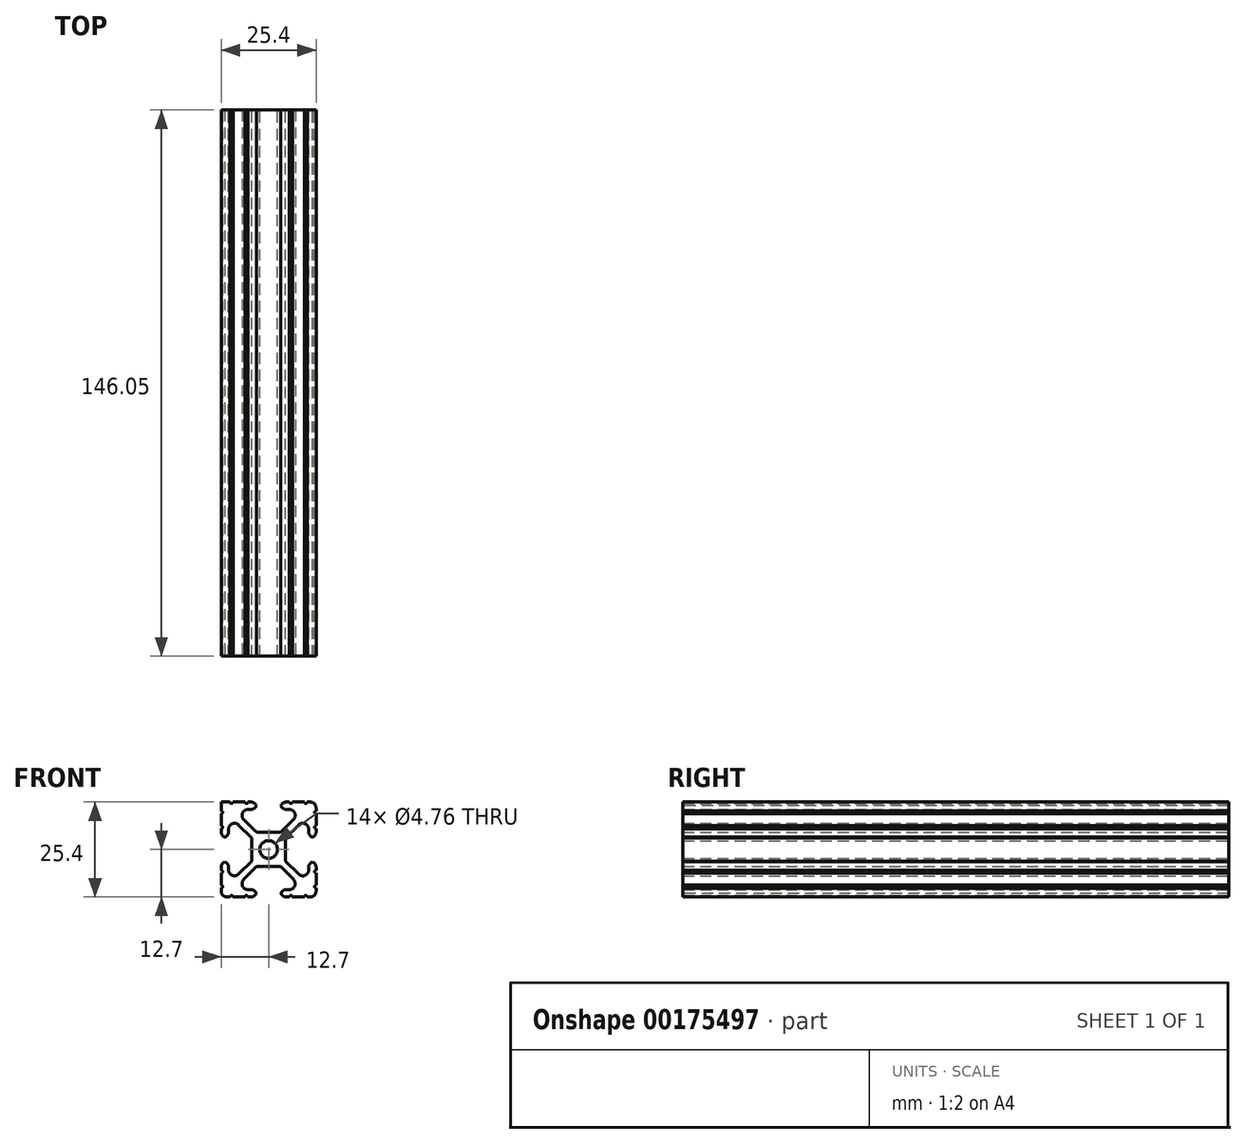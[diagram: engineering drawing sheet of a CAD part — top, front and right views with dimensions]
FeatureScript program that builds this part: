
annotation { "Feature Type Name" : "Feature", "Feature Type Description" : "" }
export const myFeature = defineFeature(function(context is Context, id is Id, definition is map)
    precondition{}
    {
        {
            var Q0;
            Q0=qCreatedBy(makeId("Front.planeOp"),FACE);
            var sketch = newSketch(context, id + "F0", { "sketchPlane" : qUnion([Q0])});
            skCircle(sketch, "E0", {"center": v(0, 0) * mm, "radius": 2.38 * mm});
            skLineSegment(sketch, "E1.bottom", {"start": v(-12.7, 12.7) * mm, "end": v(12.7, 12.7) * mm});
            skLineSegment(sketch, "E1.top", {"start": v(-12.7, -12.7) * mm, "end": v(12.7, -12.7) * mm});
            skLineSegment(sketch, "E1.left", {"start": v(-12.7, 12.7) * mm, "end": v(-12.7, -12.7) * mm});
            skLineSegment(sketch, "E1.right", {"start": v(12.7, 12.7) * mm, "end": v(12.7, -12.7) * mm});
            skPoint(sketch, "E2", {"position": v(0, 12.7) * mm});
            skLineSegment(sketch, "E3", {"start": v(0, 12.7) * mm, "end": v(-3.18, 12.7) * mm});
            skLineSegment(sketch, "E4", {"start": v(0, 12.7) * mm, "end": v(3.17, 12.7) * mm});
            skLineSegment(sketch, "E5", {"start": v(-3.18, 12.7) * mm, "end": v(-3.18, 10.72) * mm});
            skPoint(sketch, "E6", {"position": v(-12.7, 0) * mm});
            skLineSegment(sketch, "E7", {"start": v(-12.7, 0) * mm, "end": v(-12.7, 3.18) * mm});
            skLineSegment(sketch, "E8.MirrorCS", {"start": v(-12.7, 0) * mm, "end": v(-12.7, -3.18) * mm});
            skLineSegment(sketch, "E9", {"start": v(-12.7, 3.18) * mm, "end": v(-10.72, 3.18) * mm});
            skLineSegment(sketch, "E10.MirrorCS", {"start": v(-12.7, -3.18) * mm, "end": v(-10.72, -3.18) * mm});
            skLineSegment(sketch, "E11.MirrorCS", {"start": v(3.18, 12.7) * mm, "end": v(3.18, 10.72) * mm});
            skLineSegment(sketch, "E12.bottom", {"start": v(-12.7, 12.7) * mm, "end": v(-7.14, 12.7) * mm});
            skLineSegment(sketch, "E13", {"start": v(-3.18, 10.72) * mm, "end": v(-7.14, 10.72) * mm});
            skLineSegment(sketch, "E14", {"start": v(-10.72, 3.18) * mm, "end": v(-10.72, 7.14) * mm});
            skLineSegment(sketch, "E15", {"start": v(-12.7, 11.22) * mm, "end": v(-11.37, 12.7) * mm});
            skPoint(sketch, "E16", {"position": v(-1.52, -1.52) * mm});
            skPoint(sketch, "E17", {"position": v(-2.92, -2.92) * mm});
            skLineSegment(sketch, "E18", {"start": v(0, 0) * mm, "end": v(0.7, 0.7) * mm});
            skLineSegment(sketch, "E19", {"start": v(0, 0) * mm, "end": v(-0.7, -0.7) * mm});
            skLineSegment(sketch, "E20", {"start": v(-0.7, -0.7) * mm, "end": v(-12.7, 11.22) * mm});
            skLineSegment(sketch, "E21", {"start": v(-11.37, 12.7) * mm, "end": v(0.7, 0.7) * mm});
            skLineSegment(sketch, "E22.MirrorCS", {"start": v(3.18, 10.72) * mm, "end": v(7.14, 10.72) * mm});
            skLineSegment(sketch, "E23.MirrorCS", {"start": v(10.72, 3.18) * mm, "end": v(10.72, 7.14) * mm});
            skLineSegment(sketch, "E24.MirrorCS", {"start": v(12.7, 3.18) * mm, "end": v(10.72, 3.18) * mm});
            skLineSegment(sketch, "E25.MirrorCS", {"start": v(0.7, -0.7) * mm, "end": v(12.7, 11.22) * mm});
            skLineSegment(sketch, "E26.MirrorCS", {"start": v(11.37, 12.7) * mm, "end": v(-0.7, 0.7) * mm});
            skLineSegment(sketch, "E27.MirrorCS", {"start": v(3.18, -10.72) * mm, "end": v(7.14, -10.72) * mm});
            skLineSegment(sketch, "E28.MirrorCS", {"start": v(3.18, -12.7) * mm, "end": v(3.18, -10.72) * mm});
            skLineSegment(sketch, "E29.MirrorCS", {"start": v(11.37, -12.7) * mm, "end": v(-0.7, -0.7) * mm});
            skLineSegment(sketch, "E30.MirrorCS", {"start": v(0.7, 0.7) * mm, "end": v(12.7, -11.22) * mm});
            skLineSegment(sketch, "E31.MirrorCS", {"start": v(10.72, -3.18) * mm, "end": v(10.72, -7.14) * mm});
            skLineSegment(sketch, "E32.MirrorCS", {"start": v(12.7, -3.18) * mm, "end": v(10.72, -3.18) * mm});
            skLineSegment(sketch, "E33.MirrorCS", {"start": v(-3.18, -12.7) * mm, "end": v(-3.18, -10.72) * mm});
            skLineSegment(sketch, "E34.MirrorCS", {"start": v(-3.18, -10.72) * mm, "end": v(-7.14, -10.72) * mm});
            skLineSegment(sketch, "E35.MirrorCS", {"start": v(-11.37, -12.7) * mm, "end": v(0.7, -0.7) * mm});
            skLineSegment(sketch, "E36.MirrorCS", {"start": v(-0.7, 0.7) * mm, "end": v(-12.7, -11.22) * mm});
            skLineSegment(sketch, "E37.MirrorCS", {"start": v(-10.72, -3.18) * mm, "end": v(-10.72, -7.14) * mm});
            skLineSegment(sketch, "E38.bottom", {"start": v(-4.56, 4.56) * mm, "end": v(4.56, 4.56) * mm});
            skLineSegment(sketch, "E38.top", {"start": v(-4.56, -4.56) * mm, "end": v(4.56, -4.56) * mm});
            skLineSegment(sketch, "E38.left", {"start": v(-4.56, 4.56) * mm, "end": v(-4.56, -4.56) * mm});
            skLineSegment(sketch, "E38.right", {"start": v(4.56, 4.56) * mm, "end": v(4.56, -4.56) * mm});
            skPoint(sketch, "E39", {"position": v(10.32, 12.7) * mm});
            skPoint(sketch, "E40", {"position": v(9.53, 12.7) * mm});
            skArc(sketch, "E41", {"start": v(9.53, 12.7) * mm, "mid": v(9.92, 12.3) * mm, "end": v(10.32, 12.7) * mm});
            skPoint(sketch, "E42", {"position": v(6.35, 12.7) * mm});
            skPoint(sketch, "E43", {"position": v(5.56, 12.7) * mm});
            skArc(sketch, "E44", {"start": v(5.56, 12.7) * mm, "mid": v(5.95, 12.3) * mm, "end": v(6.35, 12.7) * mm});
            skArc(sketch, "E45.MirrorCS", {"start": v(9.53, -12.7) * mm, "mid": v(9.92, -12.3) * mm, "end": v(10.32, -12.7) * mm});
            skArc(sketch, "E46.MirrorCS", {"start": v(5.56, -12.7) * mm, "mid": v(5.95, -12.3) * mm, "end": v(6.35, -12.7) * mm});
            skArc(sketch, "E47.MirrorCS", {"start": v(-5.56, -12.7) * mm, "mid": v(-5.95, -12.3) * mm, "end": v(-6.35, -12.7) * mm});
            skArc(sketch, "E48.MirrorCS", {"start": v(-9.53, -12.7) * mm, "mid": v(-9.92, -12.3) * mm, "end": v(-10.32, -12.7) * mm});
            skArc(sketch, "E49.MirrorCS", {"start": v(-5.56, 12.7) * mm, "mid": v(-5.95, 12.3) * mm, "end": v(-6.35, 12.7) * mm});
            skArc(sketch, "E50.MirrorCS", {"start": v(-9.53, 12.7) * mm, "mid": v(-9.92, 12.3) * mm, "end": v(-10.32, 12.7) * mm});
            skPoint(sketch, "E51", {"position": v(12.7, 10.32) * mm});
            skPoint(sketch, "E52", {"position": v(12.7, 9.53) * mm});
            skPoint(sketch, "E53", {"position": v(12.7, 6.35) * mm});
            skPoint(sketch, "E54", {"position": v(12.7, 5.56) * mm});
            skArc(sketch, "E55", {"start": v(12.7, 10.32) * mm, "mid": v(12.3, 9.92) * mm, "end": v(12.7, 9.53) * mm});
            skArc(sketch, "E56", {"start": v(12.7, 6.35) * mm, "mid": v(12.3, 5.95) * mm, "end": v(12.7, 5.56) * mm});
            skArc(sketch, "E57.MirrorCS", {"start": v(-12.7, 10.32) * mm, "mid": v(-12.3, 9.92) * mm, "end": v(-12.7, 9.53) * mm});
            skArc(sketch, "E58.MirrorCS", {"start": v(-12.7, 6.35) * mm, "mid": v(-12.3, 5.95) * mm, "end": v(-12.7, 5.56) * mm});
            skArc(sketch, "E59.MirrorCS", {"start": v(-12.7, -6.35) * mm, "mid": v(-12.3, -5.95) * mm, "end": v(-12.7, -5.56) * mm});
            skArc(sketch, "E60.MirrorCS", {"start": v(-12.7, -10.32) * mm, "mid": v(-12.3, -9.92) * mm, "end": v(-12.7, -9.53) * mm});
            skArc(sketch, "E61.MirrorCS", {"start": v(12.7, -6.35) * mm, "mid": v(12.3, -5.95) * mm, "end": v(12.7, -5.56) * mm});
            skArc(sketch, "E62.MirrorCS", {"start": v(12.7, -10.32) * mm, "mid": v(12.3, -9.92) * mm, "end": v(12.7, -9.53) * mm});
            skLineSegment(sketch, "E63", {"start": v(-10.72, 7.14) * mm, "end": v(-10.72, 9.25) * mm});
            skLineSegment(sketch, "E64", {"start": v(-7.14, 10.72) * mm, "end": v(-9.38, 10.72) * mm});
            skLineSegment(sketch, "E65", {"start": v(7.14, 10.72) * mm, "end": v(9.38, 10.72) * mm});
            skLineSegment(sketch, "E66", {"start": v(10.72, 7.14) * mm, "end": v(10.72, 9.25) * mm});
            skLineSegment(sketch, "E67", {"start": v(7.14, -10.72) * mm, "end": v(9.38, -10.72) * mm});
            skLineSegment(sketch, "E68", {"start": v(10.72, -7.14) * mm, "end": v(10.72, -9.25) * mm});
            skLineSegment(sketch, "E69", {"start": v(-10.72, -7.14) * mm, "end": v(-10.72, -9.25) * mm});
            skLineSegment(sketch, "E70", {"start": v(-7.14, -10.72) * mm, "end": v(-9.38, -10.72) * mm});
            skSolve(sketch);
        }
        {
            var Q0;
            {var subQ0=sQuery(id+"F0.wireOp",EDGE,"E26.MirrorCS");var subQ1=sQuery(id+"F0.wireOp",EDGE,"E0");var subQ2=makeQuery(id+"F0.imprint","INTERSECT",VERTEX,{"derivedFrom":[subQ1,subQ0]});Q0=makeQuery(id+"F0.imprint","IMPRINT",FACE,{"disambiguationData":[TD([[makeQuery(id+"F0.imprint","IMPRINT",EDGE,{"disambiguationData":[TD([[subQ2,-1.0]])],"derivedFrom":subQ1}),-1.0]])]});}
            var Q1;
            {var subQ3=sQuery(id+"F0.wireOp",EDGE,"E21");var subQ5=sQuery(id+"F0.wireOp",EDGE,"E0");var subQ6=makeQuery(id+"F0.imprint","INTERSECT",VERTEX,{"derivedFrom":[subQ5,subQ3]});Q1=makeQuery(id+"F0.imprint","IMPRINT",FACE,{"disambiguationData":[TD([[makeQuery(id+"F0.imprint","IMPRINT",EDGE,{"disambiguationData":[TD([[subQ6,-1.0]])],"derivedFrom":subQ5}),-1.0]])]});}
            var Q2;
            {var subQ0=sQuery(id+"F0.wireOp",EDGE,"E20");var subQ1=sQuery(id+"F0.wireOp",EDGE,"E0");var subQ2=makeQuery(id+"F0.imprint","INTERSECT",VERTEX,{"derivedFrom":[subQ1,subQ0]});Q2=makeQuery(id+"F0.imprint","IMPRINT",FACE,{"disambiguationData":[TD([[makeQuery(id+"F0.imprint","IMPRINT",EDGE,{"disambiguationData":[TD([[subQ2,-1.0]])],"derivedFrom":subQ1}),-1.0]])]});}
            var Q3;
            {var subQ5=sQuery(id+"F0.wireOp",EDGE,"E0");var subQ7=sQuery(id+"F0.wireOp",EDGE,"E36.MirrorCS");var subQ8=makeQuery(id+"F0.imprint","INTERSECT",VERTEX,{"derivedFrom":[subQ5,subQ7]});Q3=makeQuery(id+"F0.imprint","IMPRINT",FACE,{"disambiguationData":[TD([[makeQuery(id+"F0.imprint","IMPRINT",EDGE,{"disambiguationData":[TD([[subQ8,-1.0]])],"derivedFrom":subQ5}),-1.0]])]});}
            var Q4;
            {var subQ0=sQuery(id+"F0.wireOp",EDGE,"E35.MirrorCS");var subQ1=sQuery(id+"F0.wireOp",EDGE,"E0");var subQ2=makeQuery(id+"F0.imprint","INTERSECT",VERTEX,{"derivedFrom":[subQ1,subQ0]});Q4=makeQuery(id+"F0.imprint","IMPRINT",FACE,{"disambiguationData":[TD([[makeQuery(id+"F0.imprint","IMPRINT",EDGE,{"disambiguationData":[TD([[subQ2,-1.0]])],"derivedFrom":subQ1}),-1.0]])]});}
            var Q5;
            {var subQ3=sQuery(id+"F0.wireOp",EDGE,"E29.MirrorCS");var subQ6=sQuery(id+"F0.wireOp",EDGE,"E0");var subQ9=makeQuery(id+"F0.imprint","INTERSECT",VERTEX,{"derivedFrom":[subQ6,subQ3]});Q5=makeQuery(id+"F0.imprint","IMPRINT",FACE,{"disambiguationData":[TD([[makeQuery(id+"F0.imprint","IMPRINT",EDGE,{"disambiguationData":[TD([[subQ9,-1.0]])],"derivedFrom":subQ6}),-1.0]])]});}
            var Q6;
            {var subQ0=sQuery(id+"F0.wireOp",EDGE,"E25.MirrorCS");var subQ1=sQuery(id+"F0.wireOp",EDGE,"E0");var subQ2=makeQuery(id+"F0.imprint","INTERSECT",VERTEX,{"derivedFrom":[subQ1,subQ0]});Q6=makeQuery(id+"F0.imprint","IMPRINT",FACE,{"disambiguationData":[TD([[makeQuery(id+"F0.imprint","IMPRINT",EDGE,{"disambiguationData":[TD([[subQ2,1.0]])],"derivedFrom":subQ1}),-1.0]])]});}
            var Q7;
            {var subQ3=sQuery(id+"F0.wireOp",EDGE,"E26.MirrorCS");var subQ7=sQuery(id+"F0.wireOp",EDGE,"E0");var subQ8=makeQuery(id+"F0.imprint","INTERSECT",VERTEX,{"derivedFrom":[subQ7,subQ3]});Q7=makeQuery(id+"F0.imprint","IMPRINT",FACE,{"disambiguationData":[TD([[makeQuery(id+"F0.imprint","IMPRINT",EDGE,{"disambiguationData":[TD([[subQ8,1.0]])],"derivedFrom":subQ7}),-1.0]])]});}
            var Q8;
            {var subQ1=sQuery(id+"F0.wireOp",EDGE,"E1.right");var subQ6=sQuery(id+"F0.wireOp",EDGE,"E1.bottom");var subQ7=makeQuery(id+"F0.imprint","INTERSECT",VERTEX,{"derivedFrom":[subQ6,subQ1]});Q8=makeQuery(id+"F0.imprint","IMPRINT",FACE,{"disambiguationData":[TD([[makeQuery(id+"F0.imprint","IMPRINT",EDGE,{"disambiguationData":[TD([[subQ7,1.0]])],"derivedFrom":subQ6}),-1.0]])]});}
            var Q9;
            Q9=makeQuery(id+"F0.imprint","IMPRINT",FACE,{"disambiguationData":[TD([[makeQuery(id+"F0.imprint","IMPRINT",EDGE,{"derivedFrom":sQuery(id+"F0.wireOp",EDGE,"E23.MirrorCS")}),-1.0]])]});
            var Q10;
            {var subQ0=sQuery(id+"F0.wireOp",EDGE,"E11.MirrorCS");Q10=makeQuery(id+"F0.imprint","IMPRINT",FACE,{"disambiguationData":[TD([[makeQuery(id+"F0.imprint","IMPRINT",EDGE,{"derivedFrom":subQ0}),1.0]])]});}
            var Q11;
            {var subQ4=sQuery(id+"F0.wireOp",EDGE,"E5");Q11=makeQuery(id+"F0.imprint","IMPRINT",FACE,{"disambiguationData":[TD([[makeQuery(id+"F0.imprint","IMPRINT",EDGE,{"derivedFrom":subQ4}),-1.0]])]});}
            var Q12;
            {var subQ1=sQuery(id+"F0.wireOp",EDGE,"E15");Q12=makeQuery(id+"F0.imprint","IMPRINT",FACE,{"disambiguationData":[TD([[makeQuery(id+"F0.imprint","IMPRINT",EDGE,{"derivedFrom":subQ1}),-1.0]])]});}
            var Q13;
            {var subQ3=sQuery(id+"F0.wireOp",EDGE,"E15");Q13=makeQuery(id+"F0.imprint","IMPRINT",FACE,{"disambiguationData":[TD([[makeQuery(id+"F0.imprint","IMPRINT",EDGE,{"derivedFrom":subQ3}),1.0]])]});}
            var Q14;
            {var subQ0=sQuery(id+"F0.wireOp",EDGE,"E9");Q14=makeQuery(id+"F0.imprint","IMPRINT",FACE,{"disambiguationData":[TD([[makeQuery(id+"F0.imprint","IMPRINT",EDGE,{"derivedFrom":subQ0}),1.0]])]});}
            var Q15;
            {var subQ0=sQuery(id+"F0.wireOp",EDGE,"E10.MirrorCS");Q15=makeQuery(id+"F0.imprint","IMPRINT",FACE,{"disambiguationData":[TD([[makeQuery(id+"F0.imprint","IMPRINT",EDGE,{"derivedFrom":subQ0}),-1.0]])]});}
            var Q16;
            {var subQ0=sQuery(id+"F0.wireOp",EDGE,"E10.MirrorCS");Q16=makeQuery(id+"F0.imprint","IMPRINT",FACE,{"disambiguationData":[TD([[makeQuery(id+"F0.imprint","IMPRINT",EDGE,{"derivedFrom":subQ0}),-1.0]])]});}
            var Q17;
            {var subQ4=sQuery(id+"F0.wireOp",EDGE,"E1.top");var subQ6=sQuery(id+"F0.wireOp",EDGE,"E1.left");var subQ7=makeQuery(id+"F0.imprint","INTERSECT",VERTEX,{"derivedFrom":[subQ4,subQ6]});Q17=makeQuery(id+"F0.imprint","IMPRINT",FACE,{"disambiguationData":[TD([[makeQuery(id+"F0.imprint","IMPRINT",EDGE,{"disambiguationData":[TD([[subQ7,-1.0]])],"derivedFrom":subQ4}),1.0]])]});}
            var Q18;
            {var subQ0=sQuery(id+"F0.wireOp",EDGE,"E33.MirrorCS");Q18=makeQuery(id+"F0.imprint","IMPRINT",FACE,{"disambiguationData":[TD([[makeQuery(id+"F0.imprint","IMPRINT",EDGE,{"derivedFrom":subQ0}),1.0]])]});}
            var Q19;
            Q19=makeQuery(id+"F0.imprint","IMPRINT",FACE,{"disambiguationData":[TD([[makeQuery(id+"F0.imprint","IMPRINT",EDGE,{"derivedFrom":sQuery(id+"F0.wireOp",EDGE,"E27.MirrorCS")}),-1.0]])]});
            var Q20;
            {var subQ1=sQuery(id+"F0.wireOp",EDGE,"E1.top");var subQ6=sQuery(id+"F0.wireOp",EDGE,"E1.right");var subQ7=makeQuery(id+"F0.imprint","INTERSECT",VERTEX,{"derivedFrom":[subQ1,subQ6]});Q20=makeQuery(id+"F0.imprint","IMPRINT",FACE,{"disambiguationData":[TD([[makeQuery(id+"F0.imprint","IMPRINT",EDGE,{"disambiguationData":[TD([[subQ7,1.0]])],"derivedFrom":subQ1}),1.0]])]});}
            var Q21;
            Q21=makeQuery(id+"F0.imprint","IMPRINT",FACE,{"disambiguationData":[TD([[makeQuery(id+"F0.imprint","IMPRINT",EDGE,{"derivedFrom":sQuery(id+"F0.wireOp",EDGE,"E31.MirrorCS")}),1.0]])]});
            var Q22;
            Q22=makeQuery(id+"F0.imprint","IMPRINT",FACE,{"disambiguationData":[TD([[makeQuery(id+"F0.imprint","IMPRINT",EDGE,{"derivedFrom":sQuery(id+"F0.wireOp",EDGE,"E31.MirrorCS")}),1.0]])]});
            extrude(context, id + "F1", {"entities" : qUnion([Q0, Q1, Q2, Q3, Q4, Q5, Q6, Q7, Q8, Q9, Q10, Q11, Q12, Q13, Q14, Q15, Q16, Q17, Q18, Q19, Q20, Q21, Q22]), "depth" : 146.05 * mm});
        }
        {
            var Q0;
            Q0=makeQuery(id+"F1.opExtrude","SWEPT_EDGE",EDGE,{"disambiguationData":[OSD([sQuery(id+"F0.wireOp",EDGE,"E12.bottom"),sQuery(id+"F0.wireOp",EDGE,"E12.left")])]});
            var Q1;
            Q1=makeQuery(id+"F1.opExtrude","SWEPT_EDGE",EDGE,{"disambiguationData":[OSD([sQuery(id+"F0.wireOp",EDGE,"E1.top"),sQuery(id+"F0.wireOp",EDGE,"E1.left")])]});
            var Q2;
            Q2=makeQuery(id+"F1.opExtrude","SWEPT_EDGE",EDGE,{"disambiguationData":[OSD([sQuery(id+"F0.wireOp",EDGE,"E1.top"),sQuery(id+"F0.wireOp",EDGE,"E1.right")])]});
            var Q3;
            Q3=makeQuery(id+"F1.opExtrude","SWEPT_EDGE",EDGE,{"disambiguationData":[OSD([sQuery(id+"F0.wireOp",EDGE,"E1.bottom"),sQuery(id+"F0.wireOp",EDGE,"E1.right")])]});
            var Q4;
            Q4=makeQuery(id+"F1.opExtrude","SWEPT_EDGE",EDGE,{"disambiguationData":[OSD([sQuery(id+"F0.wireOp",EDGE,"E1.left"),sQuery(id+"F0.wireOp",EDGE,"E7"),sQuery(id+"F0.wireOp",EDGE,"E9")])]});
            var Q5;
            Q5=makeQuery(id+"F1.opExtrude","SWEPT_EDGE",EDGE,{"disambiguationData":[OSD([sQuery(id+"F0.wireOp",EDGE,"E1.left"),sQuery(id+"F0.wireOp",EDGE,"E8.MirrorCS"),sQuery(id+"F0.wireOp",EDGE,"E10.MirrorCS")])]});
            var Q6;
            Q6=makeQuery(id+"F1.opExtrude","SWEPT_EDGE",EDGE,{"disambiguationData":[OSD([sQuery(id+"F0.wireOp",EDGE,"E9"),sQuery(id+"F0.wireOp",EDGE,"E14")])]});
            var Q7;
            Q7=makeQuery(id+"F1.opExtrude","SWEPT_EDGE",EDGE,{"disambiguationData":[OSD([sQuery(id+"F0.wireOp",EDGE,"E10.MirrorCS"),sQuery(id+"F0.wireOp",EDGE,"E37.MirrorCS")])]});
            var Q8;
            Q8=makeQuery(id+"F1.opExtrude","SWEPT_EDGE",EDGE,{"disambiguationData":[OSD([sQuery(id+"F0.wireOp",EDGE,"E33.MirrorCS"),sQuery(id+"F0.wireOp",EDGE,"E34.MirrorCS")])]});
            var Q9;
            Q9=makeQuery(id+"F1.opExtrude","SWEPT_EDGE",EDGE,{"disambiguationData":[OSD([sQuery(id+"F0.wireOp",EDGE,"E1.top"),sQuery(id+"F0.wireOp",EDGE,"E33.MirrorCS")])]});
            var Q10;
            Q10=makeQuery(id+"F1.opExtrude","SWEPT_EDGE",EDGE,{"disambiguationData":[OSD([sQuery(id+"F0.wireOp",EDGE,"E1.top"),sQuery(id+"F0.wireOp",EDGE,"E28.MirrorCS")])]});
            var Q11;
            Q11=makeQuery(id+"F1.opExtrude","SWEPT_EDGE",EDGE,{"disambiguationData":[OSD([sQuery(id+"F0.wireOp",EDGE,"E27.MirrorCS"),sQuery(id+"F0.wireOp",EDGE,"E28.MirrorCS")])]});
            var Q12;
            Q12=makeQuery(id+"F1.opExtrude","SWEPT_EDGE",EDGE,{"disambiguationData":[OSD([sQuery(id+"F0.wireOp",EDGE,"E1.right"),sQuery(id+"F0.wireOp",EDGE,"E32.MirrorCS")])]});
            var Q13;
            Q13=makeQuery(id+"F1.opExtrude","SWEPT_EDGE",EDGE,{"disambiguationData":[OSD([sQuery(id+"F0.wireOp",EDGE,"E1.right"),sQuery(id+"F0.wireOp",EDGE,"E24.MirrorCS")])]});
            var Q14;
            Q14=makeQuery(id+"F1.opExtrude","SWEPT_EDGE",EDGE,{"disambiguationData":[OSD([sQuery(id+"F0.wireOp",EDGE,"E31.MirrorCS"),sQuery(id+"F0.wireOp",EDGE,"E32.MirrorCS")])]});
            var Q15;
            Q15=makeQuery(id+"F1.opExtrude","SWEPT_EDGE",EDGE,{"disambiguationData":[OSD([sQuery(id+"F0.wireOp",EDGE,"E23.MirrorCS"),sQuery(id+"F0.wireOp",EDGE,"E24.MirrorCS")])]});
            var Q16;
            Q16=makeQuery(id+"F1.opExtrude","SWEPT_EDGE",EDGE,{"disambiguationData":[OSD([sQuery(id+"F0.wireOp",EDGE,"E5"),sQuery(id+"F0.wireOp",EDGE,"E13")])]});
            var Q17;
            Q17=makeQuery(id+"F1.opExtrude","SWEPT_EDGE",EDGE,{"disambiguationData":[OSD([sQuery(id+"F0.wireOp",EDGE,"E1.bottom"),sQuery(id+"F0.wireOp",EDGE,"E3"),sQuery(id+"F0.wireOp",EDGE,"E5")])]});
            var Q18;
            Q18=makeQuery(id+"F1.opExtrude","SWEPT_EDGE",EDGE,{"disambiguationData":[OSD([sQuery(id+"F0.wireOp",EDGE,"E1.bottom"),sQuery(id+"F0.wireOp",EDGE,"E4"),sQuery(id+"F0.wireOp",EDGE,"E11.MirrorCS")])]});
            var Q19;
            Q19=makeQuery(id+"F1.opExtrude","SWEPT_EDGE",EDGE,{"disambiguationData":[OSD([sQuery(id+"F0.wireOp",EDGE,"E11.MirrorCS"),sQuery(id+"F0.wireOp",EDGE,"E22.MirrorCS")])]});
            var Q20;
            Q20=makeQuery(id+"F1.opExtrude","SWEPT_EDGE",EDGE,{"disambiguationData":[OSD([sQuery(id+"F0.wireOp",EDGE,"E12.right"),sQuery(id+"F0.wireOp",EDGE,"E21")])]});
            var Q21;
            Q21=makeQuery(id+"F1.opExtrude","SWEPT_EDGE",EDGE,{"disambiguationData":[OSD([sQuery(id+"F0.wireOp",EDGE,"E12.right"),sQuery(id+"F0.wireOp",EDGE,"E13")])]});
            var Q22;
            Q22=makeQuery(id+"F1.opExtrude","SWEPT_EDGE",EDGE,{"disambiguationData":[OSD([sQuery(id+"F0.wireOp",EDGE,"E20"),sQuery(id+"F0.wireOp",EDGE,"E63")])]});
            var Q23;
            Q23=makeQuery(id+"F1.opExtrude","SWEPT_EDGE",EDGE,{"disambiguationData":[OSD([sQuery(id+"F0.wireOp",EDGE,"E26.MirrorCS"),sQuery(id+"F0.wireOp",EDGE,"E65")])]});
            var Q24;
            Q24=makeQuery(id+"F1.opExtrude","SWEPT_EDGE",EDGE,{"disambiguationData":[OSD([sQuery(id+"F0.wireOp",EDGE,"E25.MirrorCS"),sQuery(id+"F0.wireOp",EDGE,"E66")])]});
            var Q25;
            Q25=makeQuery(id+"F1.opExtrude","SWEPT_EDGE",EDGE,{"disambiguationData":[OSD([sQuery(id+"F0.wireOp",EDGE,"E30.MirrorCS"),sQuery(id+"F0.wireOp",EDGE,"E68")])]});
            var Q26;
            Q26=makeQuery(id+"F1.opExtrude","SWEPT_EDGE",EDGE,{"disambiguationData":[OSD([sQuery(id+"F0.wireOp",EDGE,"E29.MirrorCS"),sQuery(id+"F0.wireOp",EDGE,"E67")])]});
            var Q27;
            Q27=makeQuery(id+"F1.opExtrude","SWEPT_EDGE",EDGE,{"disambiguationData":[OSD([sQuery(id+"F0.wireOp",EDGE,"E35.MirrorCS"),sQuery(id+"F0.wireOp",EDGE,"E70")])]});
            var Q28;
            Q28=makeQuery(id+"F1.opExtrude","SWEPT_EDGE",EDGE,{"disambiguationData":[OSD([sQuery(id+"F0.wireOp",EDGE,"E36.MirrorCS"),sQuery(id+"F0.wireOp",EDGE,"E69")])]});
            fillet(context, id + "F2", {"entities" : qUnion([Q0, Q1, Q2, Q3, Q4, Q5, Q6, Q7, Q8, Q9, Q10, Q11, Q12, Q13, Q14, Q15, Q16, Q17, Q18, Q19, Q20, Q21, Q22, Q23, Q24, Q25, Q26, Q27, Q28]), "radius" : 1.59 * mm, "tangentPropagation" : true, "allowEdgeOverflow" : false});
        }
    });
